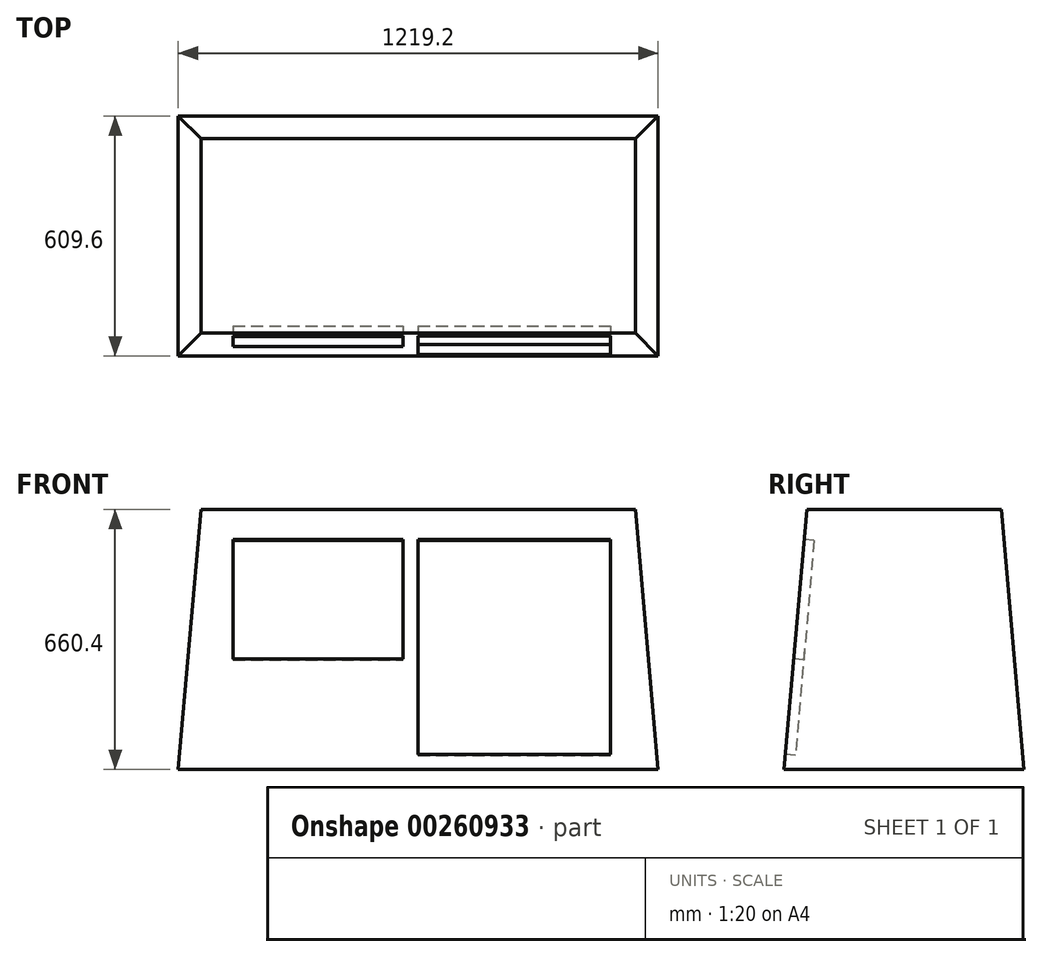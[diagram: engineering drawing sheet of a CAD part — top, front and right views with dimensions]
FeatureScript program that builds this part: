
annotation { "Feature Type Name" : "Feature", "Feature Type Description" : "" }
export const myFeature = defineFeature(function(context is Context, id is Id, definition is map)
    precondition{}
    {
        {
            var Q0;
            Q0=qCreatedBy(makeId("Top.planeOp"),FACE);
            var sketch = newSketch(context, id + "F0", { "sketchPlane" : qUnion([Q0])});
            skLineSegment(sketch, "E0.bottom", {"start": v(609.6, -304.8) * mm, "end": v(-609.6, -304.8) * mm});
            skLineSegment(sketch, "E0.top", {"start": v(609.6, 304.8) * mm, "end": v(-609.6, 304.8) * mm});
            skLineSegment(sketch, "E0.left", {"start": v(609.6, -304.8) * mm, "end": v(609.6, 304.8) * mm});
            skLineSegment(sketch, "E0.right", {"start": v(-609.6, -304.8) * mm, "end": v(-609.6, 304.8) * mm});
            skPoint(sketch, "E0.middle", {"position": v(0, 0) * mm});
            skSolve(sketch);
        }
        {
            var Q0;
            Q0 = qSketchRegion(id + "F0", true);
            extrude(context, id + "F1", {"entities" : qUnion([Q0]), "depth" : 660.4 * mm, "hasDraft" : true, "draftAngle" : 5 * degree, "draftPullDirection" : true});
        }
        {
            var Q0;
            Q0=makeQuery(id+"F1.opExtrude","SWEPT_FACE",FACE,{"disambiguationData":[OSD([sQuery(id+"F0.wireOp",EDGE,"E0.bottom")])]});
            var sketch = newSketch(context, id + "F2", { "sketchPlane" : qUnion([Q0])});
            skLineSegment(sketch, "E1.bottom", {"start": v(-469.9, 560.16) * mm, "end": v(-38.1, 560.16) * mm});
            skLineSegment(sketch, "E1.top", {"start": v(-469.9, 255.36) * mm, "end": v(-38.1, 255.36) * mm});
            skLineSegment(sketch, "E1.left", {"start": v(-469.9, 560.16) * mm, "end": v(-469.9, 255.36) * mm});
            skLineSegment(sketch, "E1.right", {"start": v(-38.1, 560.16) * mm, "end": v(-38.1, 255.36) * mm});
            skLineSegment(sketch, "E2.bottom", {"start": v(0, 560.16) * mm, "end": v(488.32, 560.16) * mm});
            skLineSegment(sketch, "E2.top", {"start": v(0, 11.53) * mm, "end": v(488.32, 11.53) * mm});
            skLineSegment(sketch, "E2.left", {"start": v(0, 560.16) * mm, "end": v(0, 11.53) * mm});
            skLineSegment(sketch, "E2.right", {"start": v(488.32, 560.16) * mm, "end": v(488.32, 11.53) * mm});
            skSolve(sketch);
        }
        {
            var Q0;
            Q0=makeQuery(id+"F2.imprint","IMPRINT",FACE,{"disambiguationData":[TD([[makeQuery(id+"F2.imprint","IMPRINT",EDGE,{"derivedFrom":sQuery(id+"F2.wireOp",EDGE,"E1.bottom")}),-1.0]])]});
            var Q1;
            Q1=makeQuery(id+"F2.imprint","IMPRINT",FACE,{"disambiguationData":[TD([[makeQuery(id+"F2.imprint","IMPRINT",EDGE,{"derivedFrom":sQuery(id+"F2.wireOp",EDGE,"E2.bottom")}),-1.0]])]});
            extrude(context, id + "F3", {"entities" : qUnion([Q0, Q1]), "operationType" : NewBodyOperationType.REMOVE, "oppositeDirection" : true, "depth" : 25.4 * mm});
        }
        {
            var Q0;
            Q0=qCreatedBy(makeId("Front.planeOp"),FACE);
            cPlane(context, id + "F4", {"entities" : qUnion([Q0]), "cplaneType" : CPlaneType.OFFSET, "offset" : 304.8 * mm, "width" : 152.4 * mm, "height" : 152.4 * mm});
        }
    });
